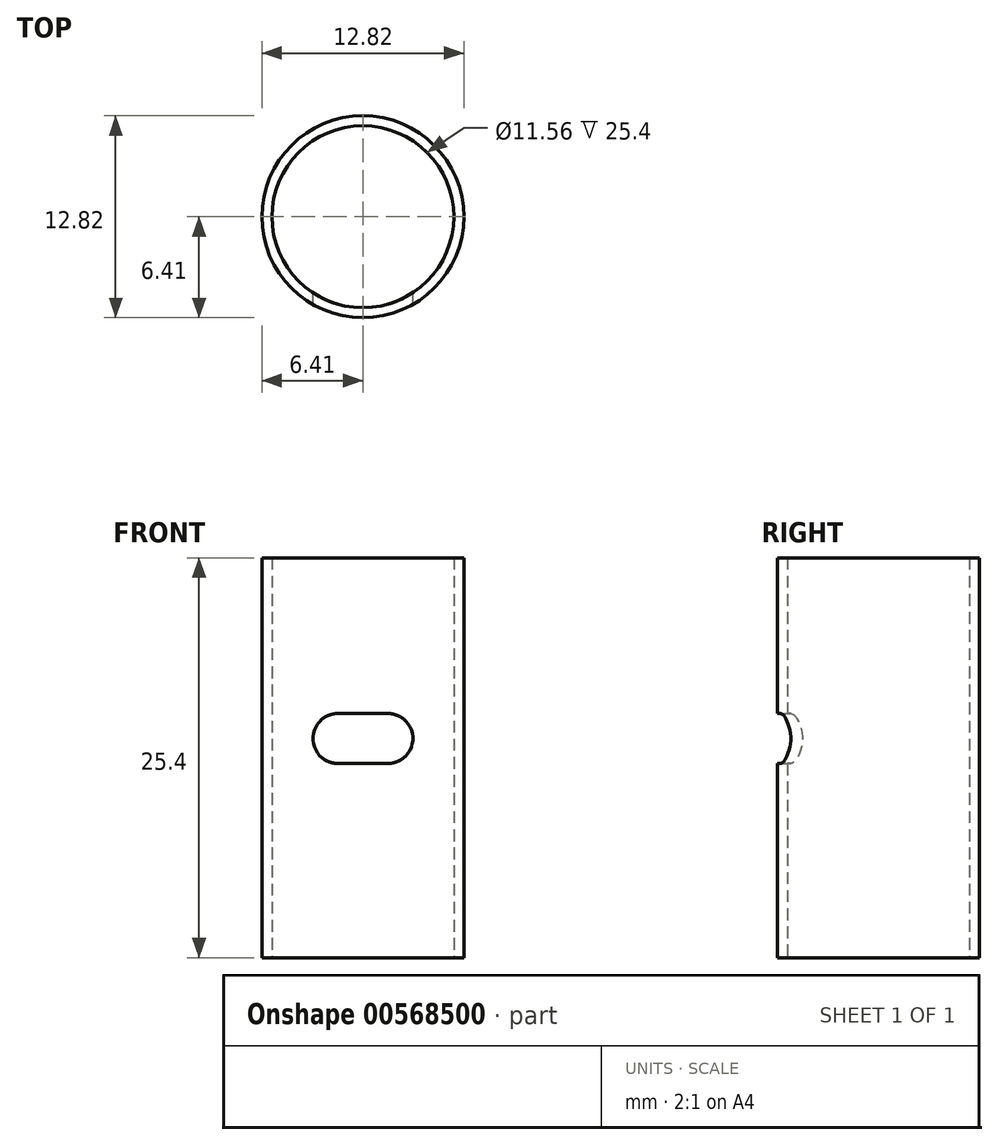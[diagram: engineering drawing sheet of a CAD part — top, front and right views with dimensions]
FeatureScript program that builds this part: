
annotation { "Feature Type Name" : "Feature", "Feature Type Description" : "" }
export const myFeature = defineFeature(function(context is Context, id is Id, definition is map)
    precondition{}
    {
        {
            var Q0;
            Q0=qCreatedBy(makeId("Top.planeOp"),FACE);
            var sketch = newSketch(context, id + "F0", { "sketchPlane" : qUnion([Q0])});
            skCircle(sketch, "E0", {"center": v(0, 0) * mm, "radius": 6.41 * mm});
            skCircle(sketch, "E1", {"center": v(0, 0) * mm, "radius": 5.78 * mm});
            skSolve(sketch);
        }
        {
            var Q0;
            Q0 = qSketchRegion(id + "F0", true);
            extrude(context, id + "F1", {"entities" : qUnion([Q0]), "depth" : 25.4 * mm, "offsetDistance" : 25.4 * mm});
        }
        {
            var Q0;
            Q0=qCreatedBy(makeId("Front.planeOp"),FACE);
            var sketch = newSketch(context, id + "F2", { "sketchPlane" : qUnion([Q0])});
            skLineSegment(sketch, "E2", {"start": v(0, 0) * mm, "end": v(0, 13.92) * mm});
            skLineSegment(sketch, "E3", {"start": v(0, 13.92) * mm, "end": v(1.59, 13.92) * mm});
            skLineSegment(sketch, "E4", {"start": v(0, 13.92) * mm, "end": v(-1.59, 13.92) * mm});
            skCircle(sketch, "E5", {"center": v(-1.59, 13.92) * mm, "radius": 1.59 * mm});
            skCircle(sketch, "E6", {"center": v(1.59, 13.92) * mm, "radius": 1.59 * mm});
            skLineSegment(sketch, "E7", {"start": v(-1.59, 15.5) * mm, "end": v(1.59, 15.5) * mm});
            skLineSegment(sketch, "E8", {"start": v(1.59, 15.5) * mm, "end": v(1.59, 12.33) * mm});
            skLineSegment(sketch, "E9", {"start": v(1.59, 12.33) * mm, "end": v(-1.59, 12.33) * mm});
            skLineSegment(sketch, "E10", {"start": v(-1.59, 12.33) * mm, "end": v(-1.59, 13.92) * mm});
            skSolve(sketch);
        }
        {
            var Q0;
            Q0 = qSketchRegion(id + "F2", true);
            extrude(context, id + "F3", {"entities" : qUnion([Q0]), "operationType" : NewBodyOperationType.REMOVE, "depth" : 25.4 * mm, "offsetDistance" : 25.4 * mm});
        }
    });
